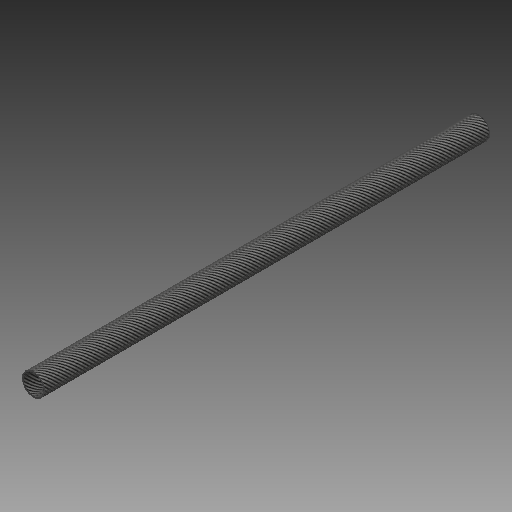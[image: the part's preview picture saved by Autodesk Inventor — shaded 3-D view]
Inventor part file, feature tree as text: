
AUTODESK INVENTOR PART (.ipt)
format: ipt  version: 2018 (Build 220112000, 112)  size: 119,808 bytes
history: native  units: in
note: dims shown in document units (in); Inventor stores cm internally (conversion verified against a paired STEP export)
features: other x3, sketch x1
ambient origin geometry x8: Origin, YZ Plane, XZ Plane, XY Plane, X Axis, Y Axis, Z Axis, Center Point
bodies: Solid1 (feature_tree)
feature tree (4):
  other  "500mm tube.ipt"
  other  "Solid1::500mm tube.ipt"
  other  "TaggingFeature1"
  sketch  "Sketch1"  dims[d0=0.3937in]
